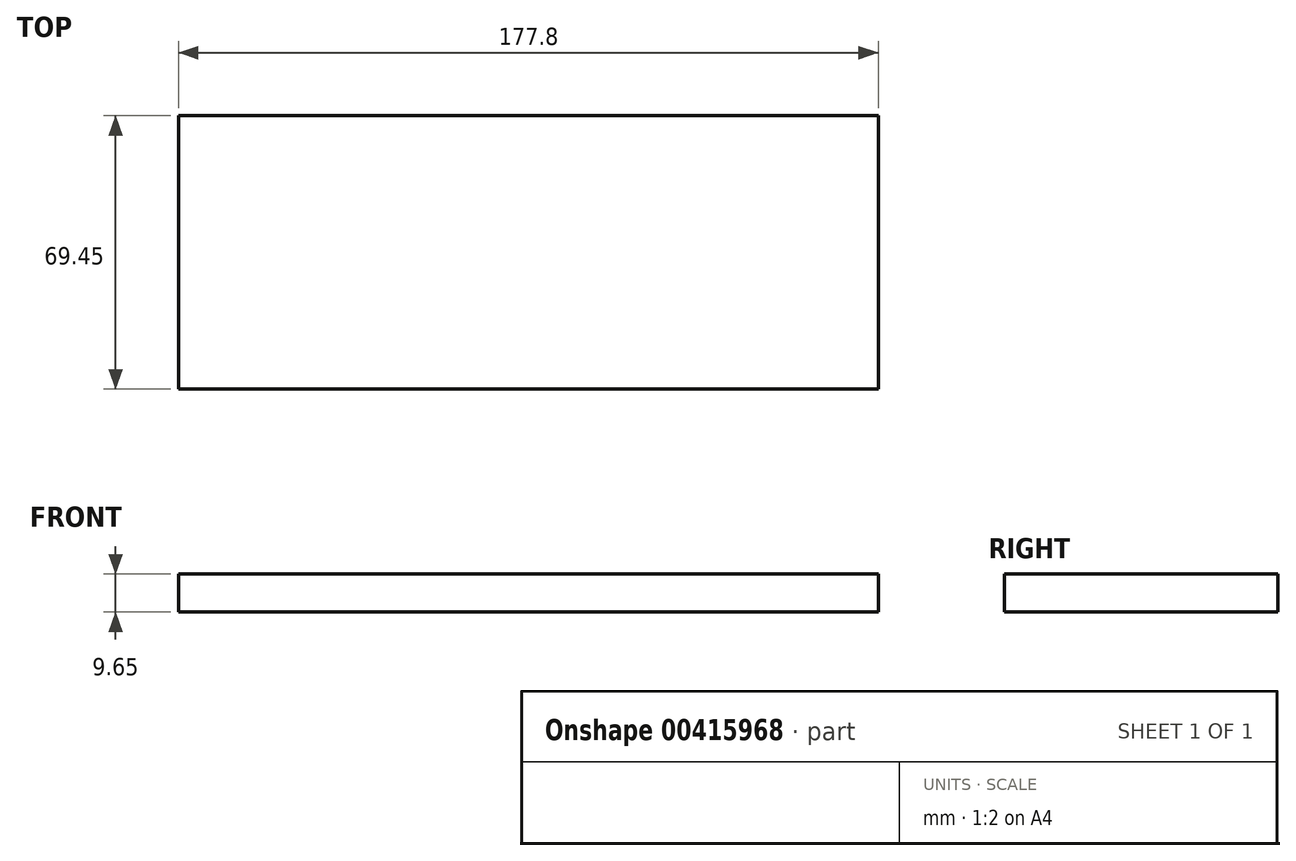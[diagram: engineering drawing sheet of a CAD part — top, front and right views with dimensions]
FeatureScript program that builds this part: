
annotation { "Feature Type Name" : "Feature", "Feature Type Description" : "" }
export const myFeature = defineFeature(function(context is Context, id is Id, definition is map)
    precondition{}
    {
        {
            var Q0;
            Q0=qCreatedBy(makeId("Front.planeOp"),FACE);
            var sketch = newSketch(context, id + "F0", { "sketchPlane" : qUnion([Q0])});
            skLineSegment(sketch, "E0", {"start": v(-88.9, 0) * mm, "end": v(-88.9, 9.65) * mm});
            skLineSegment(sketch, "E1", {"start": v(-88.9, 9.65) * mm, "end": v(88.9, 9.65) * mm});
            skLineSegment(sketch, "E2", {"start": v(-88.9, 0) * mm, "end": v(88.9, 0) * mm});
            skLineSegment(sketch, "E3", {"start": v(88.9, 9.65) * mm, "end": v(88.9, 0) * mm});
            skSolve(sketch);
        }
        {
            var Q0;
            Q0 = qSketchRegion(id + "F0", true);
            extrude(context, id + "F1", {"entities" : qUnion([Q0]), "depth" : 25.4 * mm});
        }
        {
            var Q0;
            Q0 = qSketchRegion(id + "F0", true);
            extrude(context, id + "F2", {"entities" : qUnion([Q0]), "operationType" : NewBodyOperationType.ADD, "depth" : 69.45 * mm});
        }
    });
